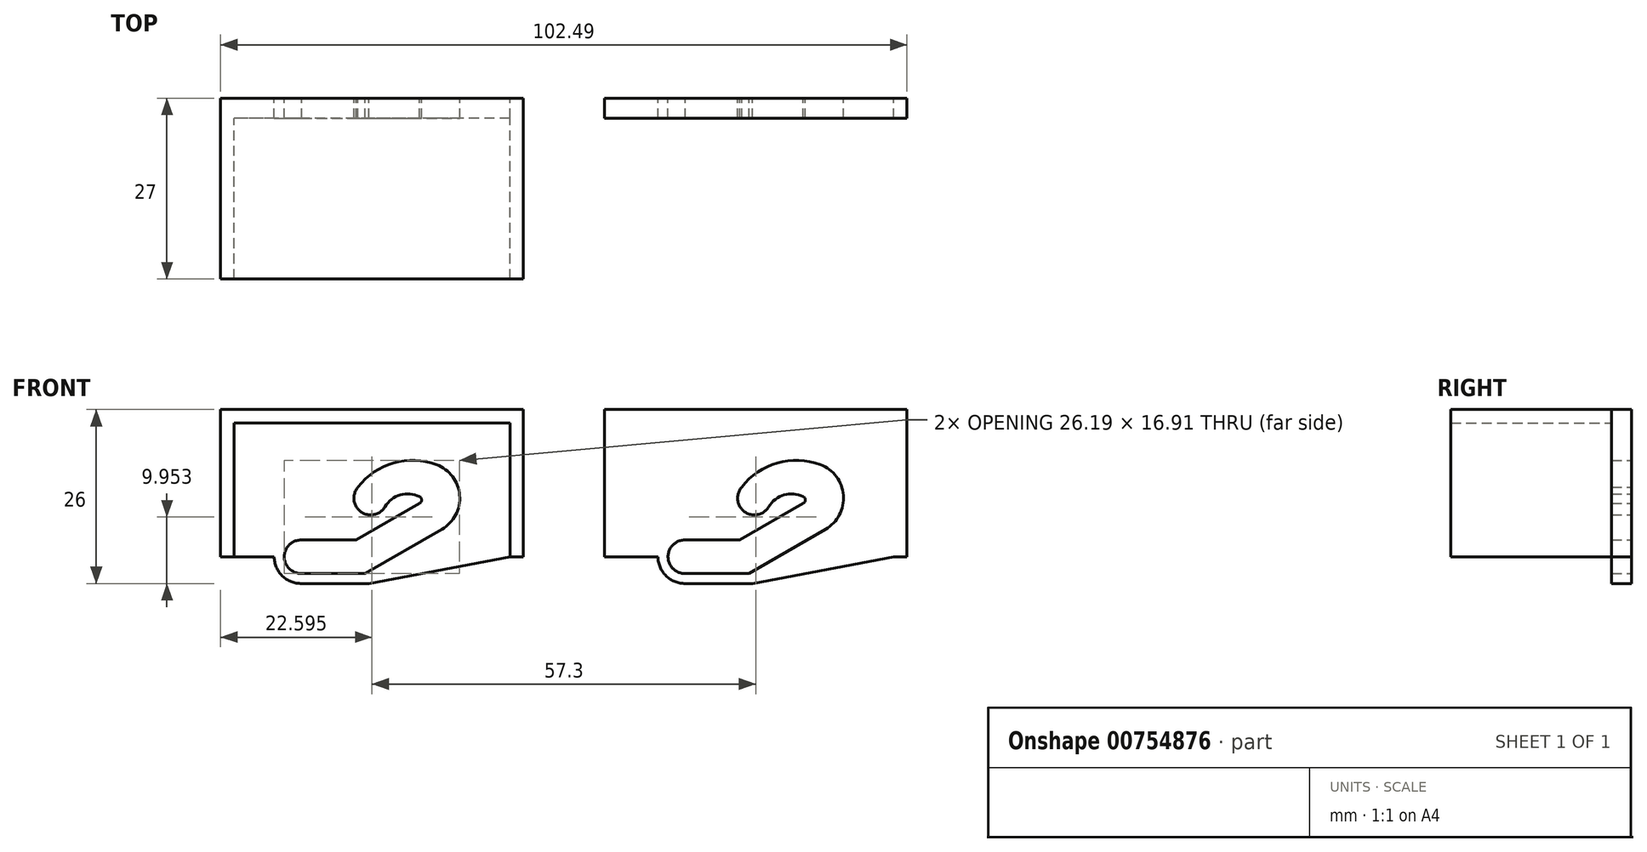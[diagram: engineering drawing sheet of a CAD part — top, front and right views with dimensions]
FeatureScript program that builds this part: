
annotation { "Feature Type Name" : "Feature", "Feature Type Description" : "" }
export const myFeature = defineFeature(function(context is Context, id is Id, definition is map)
    precondition{}
    {
        {
            var Q0;
            Q0=qCreatedBy(makeId("Front.planeOp"),FACE);
            var sketch = newSketch(context, id + "F0", { "sketchPlane" : qUnion([Q0])});
            skLineSegment(sketch, "E0.bottom", {"start": v(0, 0) * mm, "end": v(0, 0) * mm});
            skLineSegment(sketch, "E1", {"start": v(0, 0) * mm, "end": v(0, 20) * mm});
            skLineSegment(sketch, "E2", {"start": v(0, 20) * mm, "end": v(35.7, 20) * mm});
            skLineSegment(sketch, "E3", {"start": v(0, 0) * mm, "end": v(10, 0) * mm, "construction": true});
            skCircle(sketch, "E4", {"center": v(10, 0) * mm, "radius": 8 * mm, "construction": true});
            skArc(sketch, "E5", {"start": v(10, 2.5) * mm, "mid": v(7.5, -0.05) * mm, "end": v(10.1, -2.5) * mm});
            skLineSegment(sketch, "E6", {"start": v(0, 0) * mm, "end": v(0, 2) * mm});
            skArc(sketch, "E7", {"start": v(6, 0) * mm, "mid": v(7.2, -2.86) * mm, "end": v(10.1, -4) * mm});
            skLineSegment(sketch, "E8", {"start": v(10.1, -4) * mm, "end": v(20.1, -4) * mm});
            skCircle(sketch, "E9", {"center": v(15, 6.24) * mm, "radius": 2.5 * mm, "construction": true});
            skLineSegment(sketch, "E10", {"start": v(10, 2.5) * mm, "end": v(18.23, 2.5) * mm});
            skLineSegment(sketch, "E11", {"start": v(10.1, -2.5) * mm, "end": v(19.57, -2.5) * mm});
            skLineSegment(sketch, "E12", {"start": v(18.23, 2.5) * mm, "end": v(20.4, 3.75) * mm});
            skLineSegment(sketch, "E13", {"start": v(20.73, -1.83) * mm, "end": v(19.57, -2.5) * mm});
            skLineSegment(sketch, "E14", {"start": v(20.56, -1.93) * mm, "end": v(22.9, -0.58) * mm});
            skArc(sketch, "E15", {"start": v(18.51, 10.4) * mm, "mid": v(18.12, 7.72) * mm, "end": v(20.4, 6.25) * mm});
            skLineSegment(sketch, "E16", {"start": v(22.36, -0.9) * mm, "end": v(31.03, 4.12) * mm});
            skArc(sketch, "E17", {"start": v(31.03, 4.12) * mm, "mid": v(33.7, 9.18) * mm, "end": v(30.26, 13.75) * mm});
            skArc(sketch, "E18", {"start": v(30.26, 13.75) * mm, "mid": v(23.62, 13.96) * mm, "end": v(18.25, 10.03) * mm});
            skArc(sketch, "E19", {"start": v(20.4, 6.25) * mm, "mid": v(21.63, 6.57) * mm, "end": v(22.54, 7.46) * mm});
            skLineSegment(sketch, "E20", {"start": v(20.4, 3.75) * mm, "end": v(27.69, 7.96) * mm});
            skArc(sketch, "E21", {"start": v(22.54, 7.46) * mm, "mid": v(24.82, 9.23) * mm, "end": v(27.69, 9) * mm});
            skArc(sketch, "E22", {"start": v(27.69, 9) * mm, "mid": v(28.01, 8.48) * mm, "end": v(27.69, 7.96) * mm});
            skLineSegment(sketch, "E23", {"start": v(0, 0) * mm, "end": v(-2, 0) * mm});
            skLineSegment(sketch, "E24", {"start": v(-2, 0) * mm, "end": v(-2, 22) * mm});
            skLineSegment(sketch, "E25", {"start": v(-2, 22) * mm, "end": v(37.7, 22) * mm});
            skLineSegment(sketch, "E26", {"start": v(0, 0) * mm, "end": v(6, 0) * mm});
            skLineSegment(sketch, "E27", {"start": v(41.2, 9.18) * mm, "end": v(41.2, 25.92) * mm});
            skLineSegment(sketch, "E28", {"start": v(35.7, 20) * mm, "end": v(41.2, 20) * mm});
            skLineSegment(sketch, "E29", {"start": v(37.7, 22) * mm, "end": v(41.2, 22) * mm});
            skLineSegment(sketch, "E30", {"start": v(41.2, 22) * mm, "end": v(43.2, 22) * mm});
            skLineSegment(sketch, "E31", {"start": v(43.2, 22) * mm, "end": v(43.2, 0) * mm});
            skLineSegment(sketch, "E32", {"start": v(41.2, 9.18) * mm, "end": v(41.2, 0) * mm});
            skLineSegment(sketch, "E33", {"start": v(41.2, 0) * mm, "end": v(20.1, -4) * mm});
            skLineSegment(sketch, "E34", {"start": v(41.2, 0) * mm, "end": v(43.2, 0) * mm});
            skSolve(sketch);
        }
        {
            var Q0;
            {var subQ0=sQuery(id+"F0.wireOp",EDGE,"E30");Q0=makeQuery(id+"F0.imprint","IMPRINT",FACE,{"disambiguationData":[TD([[makeQuery(id+"F0.imprint","IMPRINT",EDGE,{"derivedFrom":subQ0}),-1.0]])]});}
            var Q1;
            Q1=makeQuery(id+"F0.imprint","IMPRINT",FACE,{"disambiguationData":[TD([[makeQuery(id+"F0.imprint","IMPRINT",EDGE,{"derivedFrom":sQuery(id+"F0.wireOp",EDGE,"E1")}),1.0]])]});
            var Q2;
            Q2=makeQuery(id+"F0.imprint","IMPRINT",FACE,{"disambiguationData":[TD([[makeQuery(id+"F0.imprint","IMPRINT",EDGE,{"derivedFrom":sQuery(id+"F0.wireOp",EDGE,"E1")}),-1.0]])]});
            extrude(context, id + "F1", {"entities" : qUnion([Q0, Q1, Q2]), "depth" : 3 * mm, "offsetDistance" : 25 * mm});
        }
        {
            var Q0;
            Q0=makeQuery(id+"F1.opExtrude","SWEPT_BODY",BODY,{"disambiguationData":[OSD([sQuery(id+"F0.wireOp",EDGE,"E5"),sQuery(id+"F0.wireOp",EDGE,"E7"),sQuery(id+"F0.wireOp",EDGE,"E8"),sQuery(id+"F0.wireOp",EDGE,"E10"),sQuery(id+"F0.wireOp",EDGE,"E11"),sQuery(id+"F0.wireOp",EDGE,"E12"),sQuery(id+"F0.wireOp",EDGE,"E13"),sQuery(id+"F0.wireOp",EDGE,"E14"),sQuery(id+"F0.wireOp",EDGE,"E15"),sQuery(id+"F0.wireOp",EDGE,"E16"),sQuery(id+"F0.wireOp",EDGE,"E17"),sQuery(id+"F0.wireOp",EDGE,"E18"),sQuery(id+"F0.wireOp",EDGE,"E19"),sQuery(id+"F0.wireOp",EDGE,"E20"),sQuery(id+"F0.wireOp",EDGE,"E21"),sQuery(id+"F0.wireOp",EDGE,"E22"),sQuery(id+"F0.wireOp",EDGE,"E23"),sQuery(id+"F0.wireOp",EDGE,"E24"),sQuery(id+"F0.wireOp",EDGE,"E25"),sQuery(id+"F0.wireOp",EDGE,"E26"),sQuery(id+"F0.wireOp",EDGE,"E29"),sQuery(id+"F0.wireOp",EDGE,"E30"),sQuery(id+"F0.wireOp",EDGE,"E31"),sQuery(id+"F0.wireOp",EDGE,"E33"),sQuery(id+"F0.wireOp",EDGE,"E34")])]});
            transform(context, id + "F2", {"entities" : qUnion([Q0]), "transformType" : TransformType.TRANSLATION_3D, "dx" : 57.3 * mm, "dy" : 0 * mm, "dz" : 0 * mm, "makeCopy" : true});
        }
        {
            var Q0;
            Q0=makeQuery(id+"F0.imprint","IMPRINT",FACE,{"disambiguationData":[TD([[makeQuery(id+"F0.imprint","IMPRINT",EDGE,{"derivedFrom":sQuery(id+"F0.wireOp",EDGE,"E1")}),1.0]])]});
            var Q1;
            {var subQ0=sQuery(id+"F0.wireOp",EDGE,"E30");Q1=makeQuery(id+"F0.imprint","IMPRINT",FACE,{"disambiguationData":[TD([[makeQuery(id+"F0.imprint","IMPRINT",EDGE,{"derivedFrom":subQ0}),-1.0]])]});}
            extrude(context, id + "F3", {"entities" : qUnion([Q0, Q1]), "operationType" : NewBodyOperationType.ADD, "depth" : 27 * mm, "offsetDistance" : 25 * mm});
        }
    });
